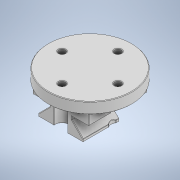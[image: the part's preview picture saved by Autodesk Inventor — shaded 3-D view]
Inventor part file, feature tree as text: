
AUTODESK INVENTOR PART (.ipt)
format: ipt  version: 2021 (Build 250183000, 183)  size: 476,672 bytes
history: native  units: mm
features: extrude x8, sketch x6, fillet x2, plane x1, mirror x1
ambient origin geometry x8: Origin, YZ Plane, XZ Plane, XY Plane, X Axis, Y Axis, Z Axis, Center Point
bodies: Solid1 (feature_tree)
feature tree (18):
  extrude  "Extrusion1"  Depth=52.5mm
  extrude  "Extrusion2"  Depth=26.25mm
  extrude  "Extrusion8"  Depth=5.0mm
  plane  "Work Plane1"
  mirror  "Mirror1"
  extrude  "Extrusion9"  TaperAngle=90.0deg  [1 undecoded]
  extrude  "Extrusion4"  Depth=10.0mm
  sketch  "Sketch6"  dims[d7=2.5mm d8=90.0deg]
  extrude  "Extrusion5"  Depth=15.0mm TaperAngle=0.0deg
  extrude  "Extrusion6"  Depth=15.0mm
  extrude  "Extrusion7"  Depth=10.0mm TaperAngle=0.0deg
  fillet  "Fillet1"  Radius=12.0mm
  fillet  "Fillet2"  Radius=6.0mm
  sketch  "Sketch1"  dims[d0=50.0mm d1=52.5mm]
  sketch  "Sketch2"  dims[d2=25.0mm d3=26.25mm]
  sketch  "Sketch4"  dims[d4=25.0mm d5=0.0mm d6=5.0mm]
  sketch  "Sketch7"  dims[d9=10.0mm d10=10.0mm]
  sketch  "Sketch8"  dims[d11=2.5mm d12=32.5mm d13=0.0mm d19=75.0mm d20=10.0mm d21=0.0mm d22=12.0mm d23=6.0mm d24=25.0mm d25=40.0mm d27=360.0deg d29=5.0mm d30=0.0mm d31=0.0mm d32=0.0mm d33=0.0mm d34=0.0mm d35=0.5mm d36=0.5mm d37=20.0mm d38=15.0mm d39=0.0mm d40=5.0mm d41=12.5mm d42=7.5mm d43=0.0mm d44=0.0mm d45=80.0mm d47=360.0deg d49=80.0mm d51=360.0deg]
note: 1 required parameter value undecoded (feature->parameter linkage not recoverable at this tier; creation-order binding heuristic only, values carry confidence <= 0.55)
